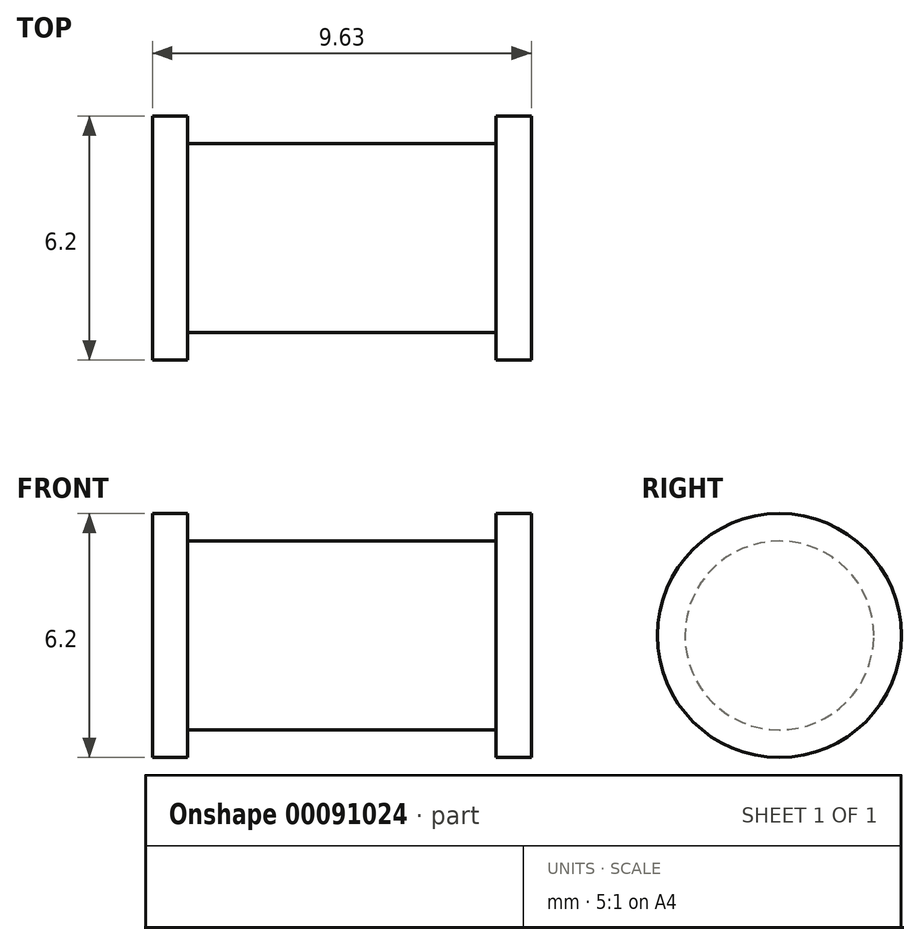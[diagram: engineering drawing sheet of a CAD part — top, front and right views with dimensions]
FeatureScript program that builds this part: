
annotation { "Feature Type Name" : "Feature", "Feature Type Description" : "" }
export const myFeature = defineFeature(function(context is Context, id is Id, definition is map)
    precondition{}
    {
        {
            var Q0;
            Q0=qCreatedBy(makeId("Front.planeOp"),FACE);
            var sketch = newSketch(context, id + "F0", { "sketchPlane" : qUnion([Q0])});
            skLineSegment(sketch, "E0", {"start": v(-18.5, 3.1) * mm, "end": v(-18.5, 6.2) * mm});
            skLineSegment(sketch, "E1", {"start": v(-18.5, 6.2) * mm, "end": v(-17.6, 6.2) * mm});
            skLineSegment(sketch, "E2", {"start": v(-17.6, 6.2) * mm, "end": v(-17.6, 5.5) * mm});
            skLineSegment(sketch, "E3", {"start": v(-17.6, 5.5) * mm, "end": v(-9.77, 5.5) * mm});
            skLineSegment(sketch, "E4", {"start": v(-9.77, 5.5) * mm, "end": v(-9.77, 6.2) * mm});
            skLineSegment(sketch, "E5", {"start": v(-9.77, 6.2) * mm, "end": v(-8.87, 6.2) * mm});
            skLineSegment(sketch, "E6", {"start": v(-8.87, 6.2) * mm, "end": v(-8.87, 3.1) * mm});
            skLineSegment(sketch, "E7", {"start": v(-18.99, 3.1) * mm, "end": v(-7.19, 3.1) * mm, "construction": true});
            skPoint(sketch, "E7.startSnap0", {"position": v(-18.5, 3.1) * mm});
            skPoint(sketch, "E8.end.orphan", {"position": v(-18.5, 0) * mm});
            skPoint(sketch, "E9.end.orphan", {"position": v(-17.6, 0) * mm});
            skPoint(sketch, "E10.orphan", {"position": v(-8.87, 0) * mm});
            skLineSegment(sketch, "E11", {"start": v(-18.5, 3.1) * mm, "end": v(-8.87, 3.1) * mm});
            skSolve(sketch);
        }
        {
            var Q0;
            Q0=makeQuery(id+"F0.imprint","IMPRINT",FACE,{"disambiguationData":[TD([[makeQuery(id+"F0.imprint","IMPRINT",EDGE,{"derivedFrom":sQuery(id+"F0.wireOp",EDGE,"E0")}),-1.0]])]});
            var Q1;
            Q1=sQuery(id+"F0.wireOp",EDGE,"E7");
            revolve(context, id + "F1", {"entities" : qUnion([Q0]), "axis" : qUnion([Q1]), "revolveType" : RevolveType.FULL});
        }
    });
